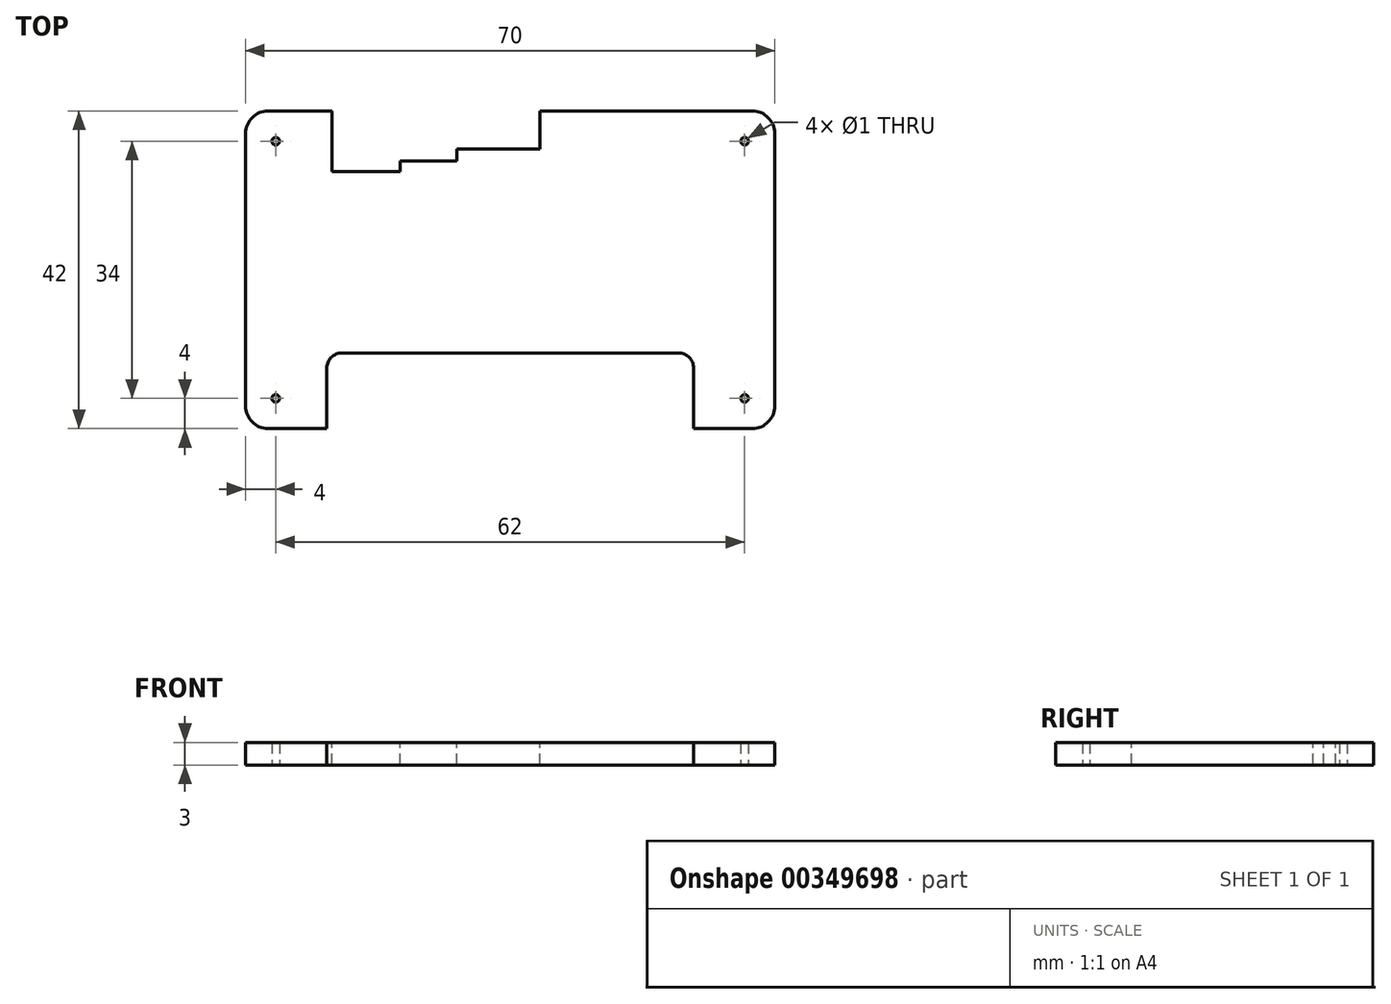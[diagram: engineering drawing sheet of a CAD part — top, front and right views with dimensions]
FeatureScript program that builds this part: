
annotation { "Feature Type Name" : "Feature", "Feature Type Description" : "" }
export const myFeature = defineFeature(function(context is Context, id is Id, definition is map)
    precondition{}
    {
        {
            var Q0;
            Q0=qCreatedBy(makeId("Top.planeOp"),FACE);
            var sketch = newSketch(context, id + "F0", { "sketchPlane" : qUnion([Q0])});
            skLineSegment(sketch, "E0.bottom", {"start": v(3, 0) * mm, "end": v(67, 0) * mm});
            skLineSegment(sketch, "E0.top", {"start": v(3, 42) * mm, "end": v(67, 42) * mm});
            skLineSegment(sketch, "E0.left", {"start": v(0, 3) * mm, "end": v(0, 39) * mm});
            skLineSegment(sketch, "E0.right", {"start": v(70, 3) * mm, "end": v(70, 39) * mm});
            skPoint(sketch, "E1.visualSharp", {"position": v(0, 42) * mm});
            skArc(sketch, "E1.filletArc", {"start": v(3, 42) * mm, "mid": v(0.88, 41.12) * mm, "end": v(0, 39) * mm});
            skPoint(sketch, "E2.visualSharp", {"position": v(70, 42) * mm});
            skArc(sketch, "E2.filletArc", {"start": v(70, 39) * mm, "mid": v(69.12, 41.12) * mm, "end": v(67, 42) * mm});
            skPoint(sketch, "E3.visualSharp", {"position": v(0, 0) * mm});
            skArc(sketch, "E3.filletArc", {"start": v(0, 3) * mm, "mid": v(0.88, 0.88) * mm, "end": v(3, 0) * mm});
            skPoint(sketch, "E4.visualSharp", {"position": v(70, 0) * mm});
            skArc(sketch, "E4.filletArc", {"start": v(67, 0) * mm, "mid": v(69.12, 0.88) * mm, "end": v(70, 3) * mm});
            skSolve(sketch);
        }
        {
            var Q0;
            Q0=makeQuery(id+"F0.imprint","IMPRINT",FACE,{"disambiguationData":[TD([[makeQuery(id+"F0.imprint","IMPRINT",EDGE,{"derivedFrom":sQuery(id+"F0.wireOp",EDGE,"E0.bottom")}),1.0]])]});
            extrude(context, id + "F1", {"entities" : qUnion([Q0]), "depth" : 3 * mm});
        }
        {
            var Q0;
            Q0=makeQuery(id+"F1.opExtrude","CAP_FACE",FACE,{"disambiguationData":[OSD([sQuery(id+"F0.wireOp",EDGE,"E0.bottom"),sQuery(id+"F0.wireOp",EDGE,"E0.top"),sQuery(id+"F0.wireOp",EDGE,"E0.left"),sQuery(id+"F0.wireOp",EDGE,"E0.right"),sQuery(id+"F0.wireOp",EDGE,"E1.filletArc"),sQuery(id+"F0.wireOp",EDGE,"E2.filletArc"),sQuery(id+"F0.wireOp",EDGE,"E3.filletArc"),sQuery(id+"F0.wireOp",EDGE,"E4.filletArc")])],"isStart":false});
            var sketch = newSketch(context, id + "F2", { "sketchPlane" : qUnion([Q0])});
            skLineSegment(sketch, "E5.bottom", {"start": v(12.75, 10) * mm, "end": v(57.25, 10) * mm});
            skLineSegment(sketch, "E5.top", {"start": v(10.75, -10) * mm, "end": v(59.25, -10) * mm});
            skLineSegment(sketch, "E5.left", {"start": v(10.75, 8) * mm, "end": v(10.75, -10) * mm});
            skLineSegment(sketch, "E5.right", {"start": v(59.25, 8) * mm, "end": v(59.25, -10) * mm});
            skPoint(sketch, "E5.middle", {"position": v(35, 0) * mm});
            skPoint(sketch, "E6.visualSharp", {"position": v(10.75, 10) * mm});
            skArc(sketch, "E6.filletArc", {"start": v(12.75, 10) * mm, "mid": v(11.34, 9.41) * mm, "end": v(10.75, 8) * mm});
            skPoint(sketch, "E7.visualSharp", {"position": v(59.25, 10) * mm});
            skArc(sketch, "E7.filletArc", {"start": v(59.25, 8) * mm, "mid": v(58.66, 9.41) * mm, "end": v(57.25, 10) * mm});
            skSolve(sketch);
        }
        {
            var Q0;
            Q0=makeQuery(id+"F2.imprint","IMPRINT",FACE,{"disambiguationData":[TD([[makeQuery(id+"F2.imprint","IMPRINT",EDGE,{"derivedFrom":sQuery(id+"F2.wireOp",EDGE,"E5.bottom")}),-1.0]])]});
            extrude(context, id + "F3", {"entities" : qUnion([Q0]), "operationType" : NewBodyOperationType.REMOVE, "endBound" : BoundingType.THROUGH_ALL, "oppositeDirection" : true, "depth" : 25 * mm});
        }
        {
            var Q0;
            Q0=makeQuery(id+"F1.opExtrude","CAP_FACE",FACE,{"disambiguationData":[OSD([sQuery(id+"F0.wireOp",EDGE,"E0.bottom"),sQuery(id+"F0.wireOp",EDGE,"E0.top"),sQuery(id+"F0.wireOp",EDGE,"E0.left"),sQuery(id+"F0.wireOp",EDGE,"E0.right"),sQuery(id+"F0.wireOp",EDGE,"E1.filletArc"),sQuery(id+"F0.wireOp",EDGE,"E2.filletArc"),sQuery(id+"F0.wireOp",EDGE,"E3.filletArc"),sQuery(id+"F0.wireOp",EDGE,"E4.filletArc")])],"isStart":false});
            var sketch = newSketch(context, id + "F4", { "sketchPlane" : qUnion([Q0])});
            skLineSegment(sketch, "E8", {"start": v(45.9, 42) * mm, "end": v(18.4, 42) * mm});
            skLineSegment(sketch, "E9.bottom", {"start": v(8.95, 42) * mm, "end": v(61.05, 42) * mm, "construction": true});
            skLineSegment(sketch, "E9.top", {"start": v(8.95, 0) * mm, "end": v(61.05, 0) * mm, "construction": true});
            skLineSegment(sketch, "E9.left", {"start": v(8.95, 42) * mm, "end": v(8.95, 0) * mm, "construction": true});
            skLineSegment(sketch, "E9.right", {"start": v(61.05, 42) * mm, "end": v(61.05, 0) * mm, "construction": true});
            skLineSegment(sketch, "E10", {"start": v(38.95, 42) * mm, "end": v(38.95, 37) * mm});
            skLineSegment(sketch, "E11", {"start": v(38.95, 37) * mm, "end": v(27.95, 37) * mm});
            skLineSegment(sketch, "E12", {"start": v(27.95, 35.4) * mm, "end": v(27.95, 37) * mm});
            skLineSegment(sketch, "E13", {"start": v(27.95, 35.4) * mm, "end": v(20.45, 35.4) * mm});
            skLineSegment(sketch, "E14", {"start": v(20.45, 34) * mm, "end": v(20.45, 35.4) * mm});
            skLineSegment(sketch, "E15", {"start": v(20.45, 34) * mm, "end": v(11.45, 34) * mm});
            skLineSegment(sketch, "E16", {"start": v(11.45, 34) * mm, "end": v(11.45, 42) * mm});
            skLineSegment(sketch, "E17", {"start": v(11.45, 42) * mm, "end": v(38.95, 42) * mm});
            skSolve(sketch);
        }
        {
            var Q0;
            {var subQ0=sQuery(id+"F4.wireOp",EDGE,"E10");Q0=makeQuery(id+"F4.imprint","IMPRINT",FACE,{"disambiguationData":[TD([[makeQuery(id+"F4.imprint","IMPRINT",EDGE,{"derivedFrom":subQ0}),-1.0]])]});}
            extrude(context, id + "F5", {"entities" : qUnion([Q0]), "operationType" : NewBodyOperationType.REMOVE, "endBound" : BoundingType.THROUGH_ALL, "oppositeDirection" : true, "depth" : 25 * mm});
        }
        {
            var Q0;
            Q0=makeQuery(id+"F1.opExtrude","CAP_FACE",FACE,{"disambiguationData":[OSD([sQuery(id+"F0.wireOp",EDGE,"E0.bottom"),sQuery(id+"F0.wireOp",EDGE,"E0.top"),sQuery(id+"F0.wireOp",EDGE,"E0.left"),sQuery(id+"F0.wireOp",EDGE,"E0.right"),sQuery(id+"F0.wireOp",EDGE,"E1.filletArc"),sQuery(id+"F0.wireOp",EDGE,"E2.filletArc"),sQuery(id+"F0.wireOp",EDGE,"E3.filletArc"),sQuery(id+"F0.wireOp",EDGE,"E4.filletArc")])],"isStart":false});
            var sketch = newSketch(context, id + "F6", { "sketchPlane" : qUnion([Q0])});
            skPoint(sketch, "E18", {"position": v(4, 4) * mm});
            skPoint(sketch, "E19", {"position": v(4, 38) * mm});
            skPoint(sketch, "E20", {"position": v(66, 38) * mm});
            skPoint(sketch, "E21", {"position": v(66, 4) * mm});
            skSolve(sketch);
        }
        {
            var Q0;
            Q0=sQuery(id+"F6.wireOp",VERTEX,"E19");
            var Q1;
            Q1=sQuery(id+"F6.wireOp",VERTEX,"E20");
            var Q2;
            Q2=sQuery(id+"F6.wireOp",VERTEX,"E21");
            var Q3;
            Q3=sQuery(id+"F6.wireOp",VERTEX,"E18");
            var Q4;
            Q4=makeQuery(id+"F1.opExtrude","SWEPT_BODY",BODY,{"disambiguationData":[OSD([sQuery(id+"F0.wireOp",EDGE,"E0.bottom"),sQuery(id+"F0.wireOp",EDGE,"E0.top"),sQuery(id+"F0.wireOp",EDGE,"E0.left"),sQuery(id+"F0.wireOp",EDGE,"E0.right"),sQuery(id+"F0.wireOp",EDGE,"E1.filletArc"),sQuery(id+"F0.wireOp",EDGE,"E2.filletArc"),sQuery(id+"F0.wireOp",EDGE,"E3.filletArc"),sQuery(id+"F0.wireOp",EDGE,"E4.filletArc")])]});
            hole(context, id + "F7", {"style" : HoleStyle.SIMPLE, "endStyle" : HoleEndStyle.THROUGH, "holeDiameter" : 1 * mm, "isTappedThrough" : true, "tappedDepth" : 12 * mm, "tapClearance" : 3, "locations" : qUnion([Q0, Q1, Q2, Q3]), "scope" : qUnion([Q4])});
        }
    });
